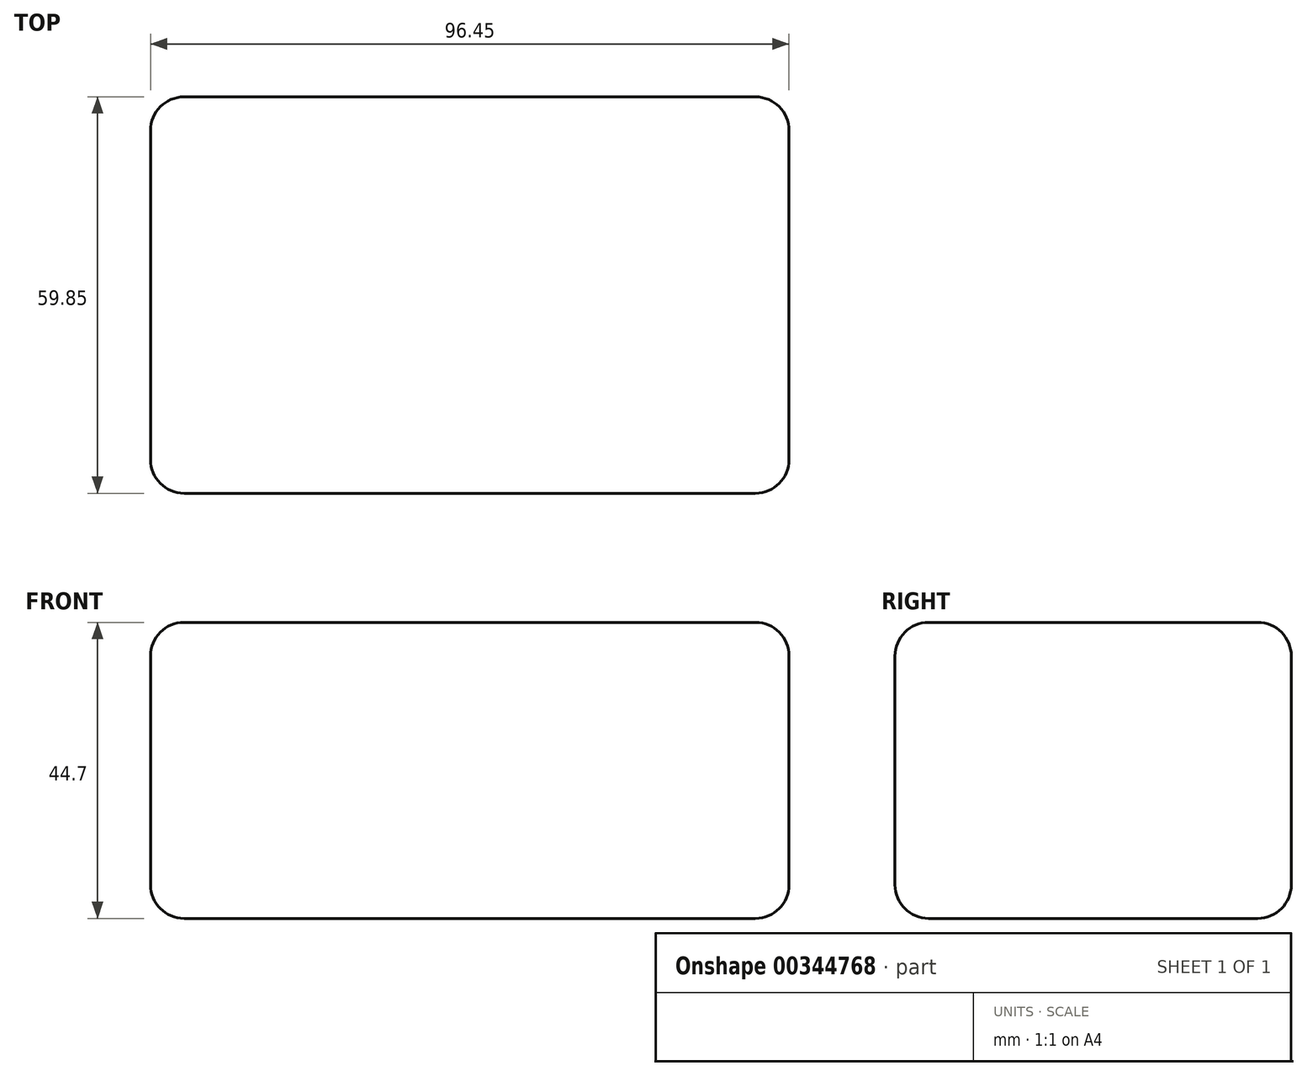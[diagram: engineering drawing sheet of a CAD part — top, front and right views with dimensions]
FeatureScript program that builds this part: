
annotation { "Feature Type Name" : "Feature", "Feature Type Description" : "" }
export const myFeature = defineFeature(function(context is Context, id is Id, definition is map)
    precondition{}
    {
        {
            var Q0;
            Q0=qCreatedBy(makeId("Top.planeOp"),FACE);
            var sketch = newSketch(context, id + "F0", { "sketchPlane" : qUnion([Q0])});
            skLineSegment(sketch, "E0.bottom", {"start": v(-35.48, 38.25) * mm, "end": v(60.97, 38.25) * mm});
            skLineSegment(sketch, "E0.top", {"start": v(-35.48, -21.6) * mm, "end": v(60.97, -21.6) * mm});
            skLineSegment(sketch, "E0.left", {"start": v(-35.48, 38.25) * mm, "end": v(-35.48, -21.6) * mm});
            skLineSegment(sketch, "E0.right", {"start": v(60.97, 38.25) * mm, "end": v(60.97, -21.6) * mm});
            skSolve(sketch);
        }
        {
            var Q0;
            Q0=makeQuery(id+"F0.imprint","IMPRINT",FACE,{"disambiguationData":[TD([[makeQuery(id+"F0.imprint","IMPRINT",EDGE,{"derivedFrom":sQuery(id+"F0.wireOp",EDGE,"E0.bottom")}),-1.0]])]});
            extrude(context, id + "F1", {"entities" : qUnion([Q0]), "oppositeDirection" : true, "depth" : 44.7 * mm});
        }
        {
            var Q0;
            Q0=makeQuery(id+"F1.opExtrude","SWEPT_FACE",FACE,{"disambiguationData":[OSD([sQuery(id+"F0.wireOp",EDGE,"E0.right")])]});
            var Q1;
            Q1=makeQuery(id+"F1.opExtrude","SWEPT_FACE",FACE,{"disambiguationData":[OSD([sQuery(id+"F0.wireOp",EDGE,"E0.bottom")])]});
            var Q2;
            Q2=makeQuery(id+"F1.opExtrude","CAP_FACE",FACE,{"disambiguationData":[OSD([sQuery(id+"F0.wireOp",EDGE,"E0.bottom"),sQuery(id+"F0.wireOp",EDGE,"E0.top"),sQuery(id+"F0.wireOp",EDGE,"E0.left"),sQuery(id+"F0.wireOp",EDGE,"E0.right")])],"isStart":false});
            var Q3;
            Q3=makeQuery(id+"F1.opExtrude","SWEPT_FACE",FACE,{"disambiguationData":[OSD([sQuery(id+"F0.wireOp",EDGE,"E0.left")])]});
            var Q4;
            Q4=makeQuery(id+"F1.opExtrude","CAP_FACE",FACE,{"disambiguationData":[OSD([sQuery(id+"F0.wireOp",EDGE,"E0.bottom"),sQuery(id+"F0.wireOp",EDGE,"E0.top"),sQuery(id+"F0.wireOp",EDGE,"E0.left"),sQuery(id+"F0.wireOp",EDGE,"E0.right")])],"isStart":true});
            var Q5;
            Q5=makeQuery(id+"F1.opExtrude","SWEPT_FACE",FACE,{"disambiguationData":[OSD([sQuery(id+"F0.wireOp",EDGE,"E0.top")])]});
            fillet(context, id + "F2", {"entities" : qUnion([Q0, Q1, Q2, Q3, Q4, Q5]), "radius" : 5.08 * mm, "tangentPropagation" : true, "allowEdgeOverflow" : false});
        }
    });
